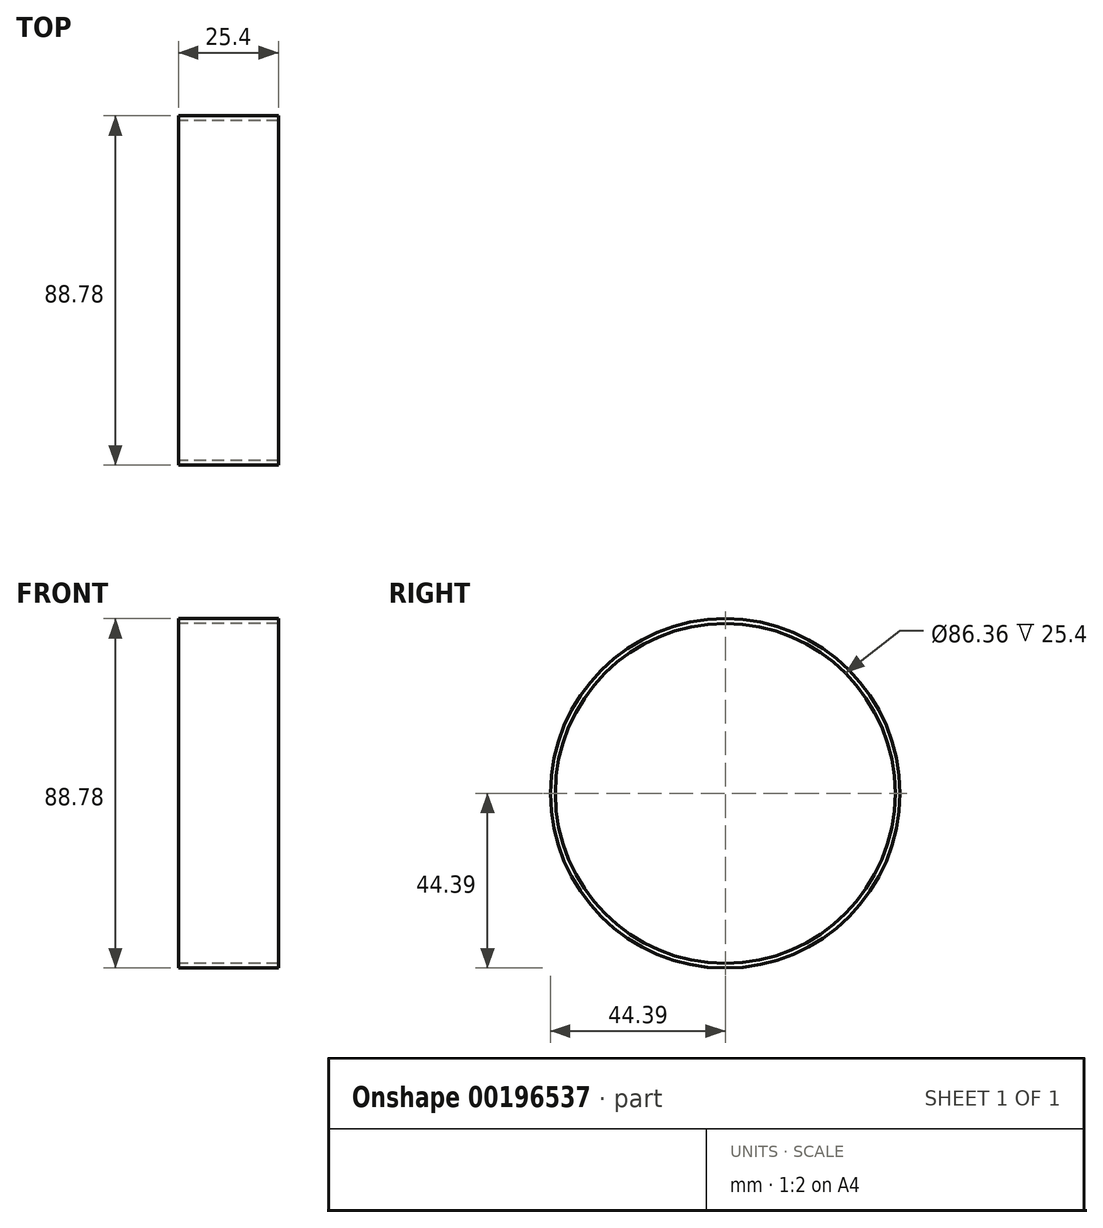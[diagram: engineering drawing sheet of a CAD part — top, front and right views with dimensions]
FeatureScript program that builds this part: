
annotation { "Feature Type Name" : "Feature", "Feature Type Description" : "" }
export const myFeature = defineFeature(function(context is Context, id is Id, definition is map)
    precondition{}
    {
        {
            var Q0;
            Q0=qCreatedBy(makeId("Right.planeOp"),FACE);
            var sketch = newSketch(context, id + "F0", { "sketchPlane" : qUnion([Q0])});
            skCircle(sketch, "E0", {"center": v(0, 0) * mm, "radius": 44.39 * mm});
            skCircle(sketch, "E1", {"center": v(0, 0) * mm, "radius": 43.18 * mm});
            skSolve(sketch);
        }
        {
            var Q0;
            Q0 = qSketchRegion(id + "F0", true);
            extrude(context, id + "F1", {"entities" : qUnion([Q0]), "depth" : 25.4 * mm});
        }
    });
